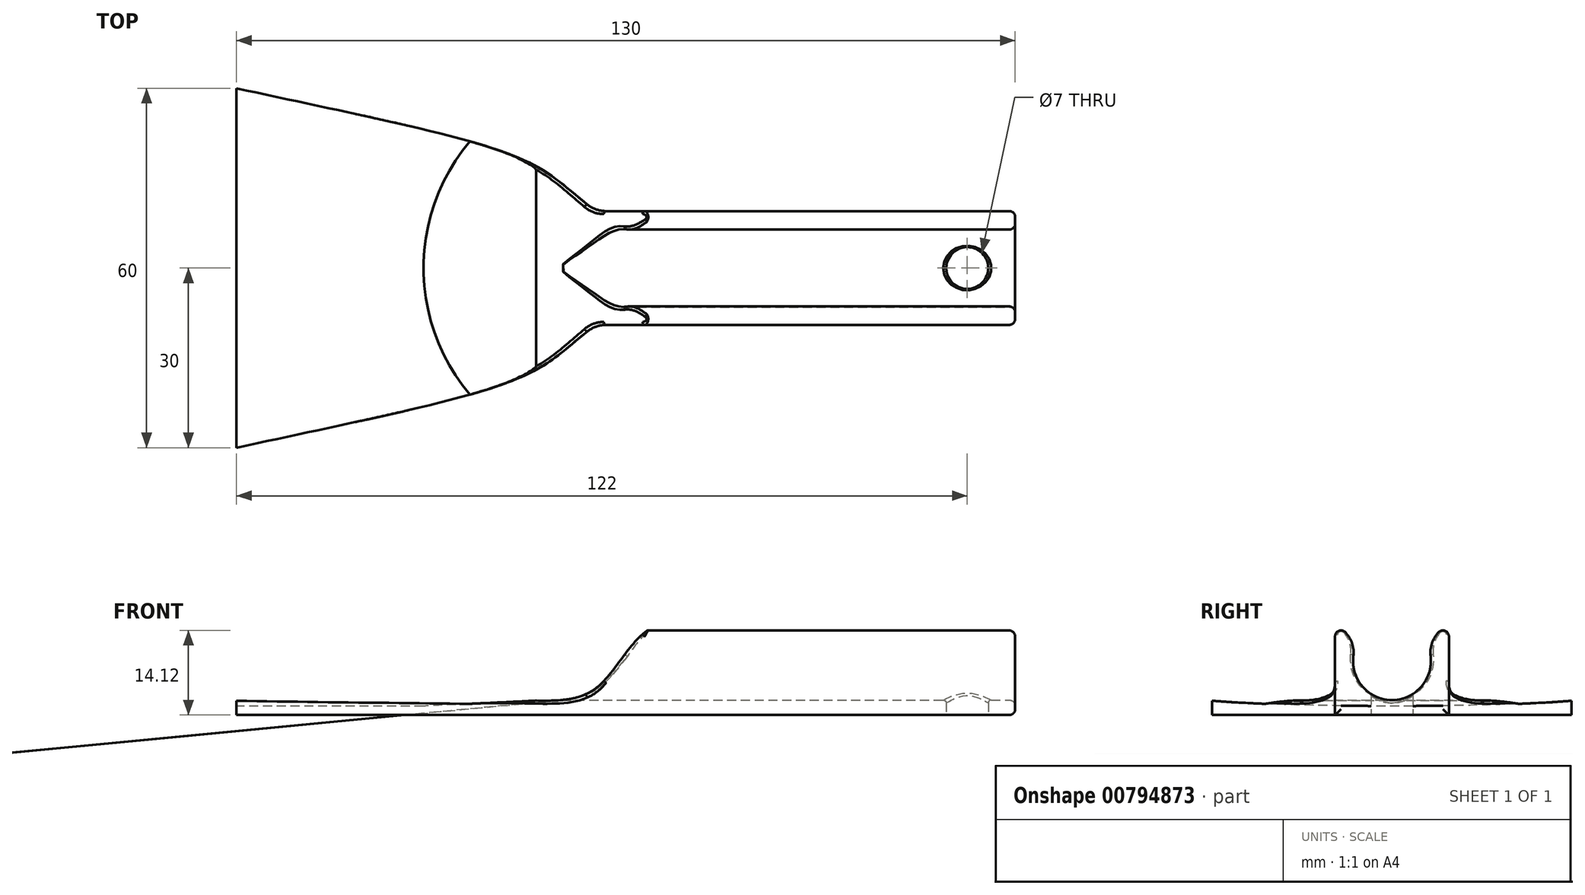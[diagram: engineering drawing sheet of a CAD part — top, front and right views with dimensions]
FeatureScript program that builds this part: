
annotation { "Feature Type Name" : "Feature", "Feature Type Description" : "" }
export const myFeature = defineFeature(function(context is Context, id is Id, definition is map)
    precondition{}
    {
        {
            var Q0;
            Q0=qCreatedBy(makeId("Top.planeOp"),FACE);
            var sketch = newSketch(context, id + "F0", { "sketchPlane" : qUnion([Q0])});
            skLineSegment(sketch, "E0.bottom", {"start": v(-35, 9.5) * mm, "end": v(35, 9.5) * mm});
            skLineSegment(sketch, "E0.top", {"start": v(-35, -9.5) * mm, "end": v(35, -9.5) * mm});
            skLineSegment(sketch, "E0.left", {"start": v(-35, 9.5) * mm, "end": v(-35, -9.5) * mm});
            skLineSegment(sketch, "E0.right", {"start": v(35, 9.5) * mm, "end": v(35, -9.5) * mm});
            skSolve(sketch);
        }
        {
            var Q0;
            Q0=makeQuery(id+"F0.imprint","IMPRINT",FACE,{"disambiguationData":[TD([[makeQuery(id+"F0.imprint","IMPRINT",EDGE,{"derivedFrom":sQuery(id+"F0.wireOp",EDGE,"E0.bottom")}),-1.0]])]});
            extrude(context, id + "F1", {"entities" : qUnion([Q0]), "depth" : 15 * mm, "offsetDistance" : 25 * mm});
        }
        {
            var Q0;
            Q0=qCreatedBy(makeId("Top.planeOp"),FACE);
            var sketch = newSketch(context, id + "F2", { "sketchPlane" : qUnion([Q0])});
            skFitSpline(sketch, "E1", {"points": [v(-35, 9.5) * mm, v(-45, 17) * mm, v(-95, 30) * mm], "startDerivative": vector(-36.4, 27.3) * mm, "endDerivative": vector(-124.24, 26.85) * mm});
            skLineSegment(sketch, "E2", {"start": v(-95, 30) * mm, "end": v(-95, 0) * mm});
            skLineSegment(sketch, "E3", {"start": v(-95, 0) * mm, "end": v(-35, 0) * mm});
            skLineSegment(sketch, "E4", {"start": v(-35, 0) * mm, "end": v(-35, 9.5) * mm});
            skSolve(sketch);
        }
        {
            var Q0;
            Q0=makeQuery(id+"F2.imprint","IMPRINT",FACE,{"disambiguationData":[TD([[makeQuery(id+"F2.imprint","IMPRINT",EDGE,{"derivedFrom":sQuery(id+"F2.wireOp",EDGE,"E1")}),1.0]])]});
            extrude(context, id + "F3", {"entities" : qUnion([Q0]), "operationType" : NewBodyOperationType.ADD, "depth" : 15 * mm, "offsetDistance" : 25 * mm});
        }
        {
            var Q0;
            Q0=makeQuery(id+"F1.opExtrude","SWEPT_BODY",BODY,{"disambiguationData":[OSD([sQuery(id+"F0.wireOp",EDGE,"E0.bottom"),sQuery(id+"F0.wireOp",EDGE,"E0.top"),sQuery(id+"F0.wireOp",EDGE,"E0.left"),sQuery(id+"F0.wireOp",EDGE,"E0.right")])]});
            var Q1;
            Q1=qCreatedBy(makeId("Front.planeOp"),FACE);
            mirror(context, id + "F4", {"operationType" : NewBodyOperationType.ADD, "entities" : qUnion([Q0]), "mirrorPlane" : qUnion([Q1])});
        }
        {
            var Q0;
            Q0=qCreatedBy(makeId("Front.planeOp"),FACE);
            var sketch = newSketch(context, id + "F5", { "sketchPlane" : qUnion([Q0])});
            skLineSegment(sketch, "E5", {"start": v(-50, 2.5) * mm, "end": v(-95, 2.5) * mm});
            skLineSegment(sketch, "E6", {"start": v(-95, 2.5) * mm, "end": v(-95, 15) * mm});
            skLineSegment(sketch, "E7", {"start": v(-95, 15) * mm, "end": v(-25, 15) * mm});
            skLineSegment(sketch, "E8", {"start": v(-50, 2.5) * mm, "end": v(-25, 15) * mm, "construction": true});
            skLineSegment(sketch, "E9", {"start": v(-37.5, 8.75) * mm, "end": v(-35.26, 4.28) * mm, "construction": true});
            skFitSpline(sketch, "E10", {"points": [v(-50, 2.5) * mm, v(-35.26, 4.28) * mm, v(-25, 15) * mm], "startDerivative": vector(36, 0) * mm, "endDerivative": vector(26.83, 13.42) * mm});
            skSolve(sketch);
        }
        {
            var Q0;
            Q0 = qSketchRegion(id + "F5", true);
            extrude(context, id + "F6", {"entities" : qUnion([Q0]), "operationType" : NewBodyOperationType.REMOVE, "endBound" : BoundingType.THROUGH_ALL, "oppositeDirection" : true, "depth" : 25 * mm, "offsetDistance" : 25 * mm, "hasSecondDirection" : true, "secondDirectionBound" : SecondDirectionBoundingType.THROUGH_ALL, "secondDirectionOppositeDirection" : false, "secondDirectionDepth" : 25 * mm});
        }
        {
            var Q0;
            Q0=makeQuery(id+"F1.opExtrude","SWEPT_FACE",FACE,{"disambiguationData":[OSD([sQuery(id+"F0.wireOp",EDGE,"E0.right")])]});
            var sketch = newSketch(context, id + "F7", { "sketchPlane" : qUnion([Q0])});
            skCircle(sketch, "E11", {"center": v(0, 9) * mm, "radius": 6.5 * mm});
            skSolve(sketch);
        }
        {
            var Q0;
            {var subQ0=sQuery(id+"F7.wireOp",EDGE,"E11");var subQ1=makeQuery(id+"F1.opExtrude","CAP_EDGE",EDGE,{"disambiguationData":[OSD([sQuery(id+"F0.wireOp",EDGE,"E0.right")])],"isStart":false});var subQ2=makeQuery(id+"F7.imprint","INTERSECT",VERTEX,{"disambiguationData":[OD(0.0)],"derivedFrom":[subQ1,subQ0]});Q0=makeQuery(id+"F7.imprint","IMPRINT",FACE,{"disambiguationData":[TD([[makeQuery(id+"F7.imprint","IMPRINT",EDGE,{"disambiguationData":[TD([[subQ2,1.0]])],"derivedFrom":subQ0}),1.0]])]});}
            var Q1;
            {var subQ0=sQuery(id+"F7.wireOp",EDGE,"E11");var subQ1=makeQuery(id+"F1.opExtrude","CAP_EDGE",EDGE,{"disambiguationData":[OSD([sQuery(id+"F0.wireOp",EDGE,"E0.right")])],"isStart":false});var subQ2=makeQuery(id+"F7.imprint","INTERSECT",VERTEX,{"disambiguationData":[OD(0.0)],"derivedFrom":[subQ1,subQ0]});Q1=makeQuery(id+"F7.imprint","IMPRINT",FACE,{"disambiguationData":[TD([[makeQuery(id+"F7.imprint","IMPRINT",EDGE,{"disambiguationData":[TD([[subQ2,-1.0]])],"derivedFrom":subQ0}),1.0]])]});}
            extrude(context, id + "F8", {"entities" : qUnion([Q0, Q1]), "operationType" : NewBodyOperationType.REMOVE, "endBound" : BoundingType.THROUGH_ALL, "oppositeDirection" : true, "depth" : 25 * mm, "offsetDistance" : 25 * mm});
        }
        {
            var Q0;
            {var subQ0=makeQuery(id+"F3.boolean.opBoolean","MERGE",FACE,{"derivedFrom":[makeQuery(id+"F1.opExtrude","CAP_FACE",FACE,{"disambiguationData":[OSD([sQuery(id+"F0.wireOp",EDGE,"E0.bottom"),sQuery(id+"F0.wireOp",EDGE,"E0.top"),sQuery(id+"F0.wireOp",EDGE,"E0.left"),sQuery(id+"F0.wireOp",EDGE,"E0.right")])],"isStart":false}),makeQuery(id+"F3.opExtrude","CAP_FACE",FACE,{"disambiguationData":[OSD([sQuery(id+"F2.wireOp",EDGE,"E1"),sQuery(id+"F2.wireOp",EDGE,"E2"),sQuery(id+"F2.wireOp",EDGE,"E3"),sQuery(id+"F2.wireOp",EDGE,"E4")])],"isStart":false})]});Q0=makeQuery(id+"F8.boolean.opBoolean","INTERSECT",EDGE,{"disambiguationData":[OD(1.0)],"derivedFrom":[makeQuery(id+"F4.boolean.opBoolean","MERGE",FACE,{"derivedFrom":[subQ0,makeQuery(id+"F4.opPattern","COPY",FACE,{"derivedFrom":subQ0,"instanceName":"1"})]}),makeQuery(id+"F8.opExtrude","SWEPT_FACE",FACE,{"disambiguationData":[OSD([sQuery(id+"F7.wireOp",EDGE,"E11")])]})]});}
            var Q1;
            {var subQ0=makeQuery(id+"F3.boolean.opBoolean","MERGE",FACE,{"derivedFrom":[makeQuery(id+"F1.opExtrude","CAP_FACE",FACE,{"disambiguationData":[OSD([sQuery(id+"F0.wireOp",EDGE,"E0.bottom"),sQuery(id+"F0.wireOp",EDGE,"E0.top"),sQuery(id+"F0.wireOp",EDGE,"E0.left"),sQuery(id+"F0.wireOp",EDGE,"E0.right")])],"isStart":false}),makeQuery(id+"F3.opExtrude","CAP_FACE",FACE,{"disambiguationData":[OSD([sQuery(id+"F2.wireOp",EDGE,"E1"),sQuery(id+"F2.wireOp",EDGE,"E2"),sQuery(id+"F2.wireOp",EDGE,"E3"),sQuery(id+"F2.wireOp",EDGE,"E4")])],"isStart":false})]});Q1=makeQuery(id+"F8.boolean.opBoolean","INTERSECT",EDGE,{"disambiguationData":[OD(0.0)],"derivedFrom":[makeQuery(id+"F4.boolean.opBoolean","MERGE",FACE,{"derivedFrom":[subQ0,makeQuery(id+"F4.opPattern","COPY",FACE,{"derivedFrom":subQ0,"instanceName":"1"})]}),makeQuery(id+"F8.opExtrude","SWEPT_FACE",FACE,{"disambiguationData":[OSD([sQuery(id+"F7.wireOp",EDGE,"E11")])]})]});}
            fillet(context, id + "F9", {"entities" : qUnion([Q0, Q1]), "radius" : 5 * mm, "tangentPropagation" : true, "allowEdgeOverflow" : false});
        }
        {
            var Q0;
            {var subQ0=sQuery(id+"F0.wireOp",EDGE,"E0.left");Q0=makeQuery(id+"F4.boolean.opBoolean","MERGE",EDGE,{"derivedFrom":[makeQuery(id+"F1.opExtrude","SWEPT_EDGE",EDGE,{"disambiguationData":[OSD([sQuery(id+"F0.wireOp",EDGE,"E0.top"),subQ0])]}),makeQuery(id+"F4.opPattern","COPY",EDGE,{"derivedFrom":makeQuery(id+"F3.boolean.opBoolean","MERGE",EDGE,{"derivedFrom":[makeQuery(id+"F1.opExtrude","SWEPT_EDGE",EDGE,{"disambiguationData":[OSD([sQuery(id+"F0.wireOp",EDGE,"E0.bottom"),subQ0])]}),makeQuery(id+"F3.opExtrude","SWEPT_EDGE",EDGE,{"disambiguationData":[OSD([sQuery(id+"F2.wireOp",EDGE,"E1"),sQuery(id+"F2.wireOp",EDGE,"E4")])]})]}),"instanceName":"1"})]});}
            var Q1;
            Q1=makeQuery(id+"F3.boolean.opBoolean","MERGE",EDGE,{"derivedFrom":[makeQuery(id+"F1.opExtrude","SWEPT_EDGE",EDGE,{"disambiguationData":[OSD([sQuery(id+"F0.wireOp",EDGE,"E0.bottom"),sQuery(id+"F0.wireOp",EDGE,"E0.left")])]}),makeQuery(id+"F3.opExtrude","SWEPT_EDGE",EDGE,{"disambiguationData":[OSD([sQuery(id+"F2.wireOp",EDGE,"E1"),sQuery(id+"F2.wireOp",EDGE,"E4")])]})]});
            fillet(context, id + "F10", {"entities" : qUnion([Q0, Q1]), "radius" : 5 * mm, "tangentPropagation" : true, "allowEdgeOverflow" : false});
        }
        {
            var Q0;
            {var subQ0=sQuery(id+"F0.wireOp",EDGE,"E0.top");var subQ1=makeQuery(id+"F3.boolean.opBoolean","MERGE",FACE,{"derivedFrom":[makeQuery(id+"F1.opExtrude","CAP_FACE",FACE,{"disambiguationData":[OSD([sQuery(id+"F0.wireOp",EDGE,"E0.bottom"),subQ0,sQuery(id+"F0.wireOp",EDGE,"E0.left"),sQuery(id+"F0.wireOp",EDGE,"E0.right")])],"isStart":false}),makeQuery(id+"F3.opExtrude","CAP_FACE",FACE,{"disambiguationData":[OSD([sQuery(id+"F2.wireOp",EDGE,"E1"),sQuery(id+"F2.wireOp",EDGE,"E2"),sQuery(id+"F2.wireOp",EDGE,"E3"),sQuery(id+"F2.wireOp",EDGE,"E4")])],"isStart":false})]});Q0=makeQuery(id+"F9.opFillet","BLEND_EDGE",EDGE,{"blendedFrom":[makeQuery(id+"F8.boolean.opBoolean","INTERSECT",EDGE,{"disambiguationData":[OD(1.0)],"derivedFrom":[makeQuery(id+"F4.boolean.opBoolean","MERGE",FACE,{"derivedFrom":[subQ1,makeQuery(id+"F4.opPattern","COPY",FACE,{"derivedFrom":subQ1,"instanceName":"1"})]}),makeQuery(id+"F8.opExtrude","SWEPT_FACE",FACE,{"disambiguationData":[OSD([sQuery(id+"F7.wireOp",EDGE,"E11")])]})]}),makeQuery(id+"F1.opExtrude","SWEPT_FACE",FACE,{"disambiguationData":[OSD([subQ0])]})],"blendedInto":[makeQuery(id+"F1.opExtrude","SWEPT_FACE",FACE,{"disambiguationData":[OSD([subQ0])]})]});}
            var Q1;
            {var subQ0=sQuery(id+"F0.wireOp",EDGE,"E0.bottom");var subQ1=makeQuery(id+"F3.boolean.opBoolean","MERGE",FACE,{"derivedFrom":[makeQuery(id+"F1.opExtrude","CAP_FACE",FACE,{"disambiguationData":[OSD([subQ0,sQuery(id+"F0.wireOp",EDGE,"E0.top"),sQuery(id+"F0.wireOp",EDGE,"E0.left"),sQuery(id+"F0.wireOp",EDGE,"E0.right")])],"isStart":false}),makeQuery(id+"F3.opExtrude","CAP_FACE",FACE,{"disambiguationData":[OSD([sQuery(id+"F2.wireOp",EDGE,"E1"),sQuery(id+"F2.wireOp",EDGE,"E2"),sQuery(id+"F2.wireOp",EDGE,"E3"),sQuery(id+"F2.wireOp",EDGE,"E4")])],"isStart":false})]});Q1=makeQuery(id+"F9.opFillet","BLEND_EDGE",EDGE,{"blendedFrom":[makeQuery(id+"F8.boolean.opBoolean","INTERSECT",EDGE,{"disambiguationData":[OD(0.0)],"derivedFrom":[makeQuery(id+"F4.boolean.opBoolean","MERGE",FACE,{"derivedFrom":[subQ1,makeQuery(id+"F4.opPattern","COPY",FACE,{"derivedFrom":subQ1,"instanceName":"1"})]}),makeQuery(id+"F8.opExtrude","SWEPT_FACE",FACE,{"disambiguationData":[OSD([sQuery(id+"F7.wireOp",EDGE,"E11")])]})]}),makeQuery(id+"F1.opExtrude","SWEPT_FACE",FACE,{"disambiguationData":[OSD([subQ0])]})],"blendedInto":[makeQuery(id+"F1.opExtrude","SWEPT_FACE",FACE,{"disambiguationData":[OSD([subQ0])]})]});}
            fillet(context, id + "F11", {"entities" : qUnion([Q0, Q1]), "radius" : 1 * mm, "tangentPropagation" : true, "allowEdgeOverflow" : false});
        }
        {
            var Q0;
            Q0=qCreatedBy(makeId("Top.planeOp"),FACE);
            var sketch = newSketch(context, id + "F12", { "sketchPlane" : qUnion([Q0])});
            skCircle(sketch, "E12", {"center": v(27, 0) * mm, "radius": 3.5 * mm});
            skSolve(sketch);
        }
        {
            var Q0;
            Q0=makeQuery(id+"F12.imprint","IMPRINT",FACE,{"disambiguationData":[TD([[makeQuery(id+"F12.imprint","IMPRINT",EDGE,{"derivedFrom":sQuery(id+"F12.wireOp",EDGE,"E12")}),1.0]])]});
            extrude(context, id + "F13", {"entities" : qUnion([Q0]), "operationType" : NewBodyOperationType.REMOVE, "endBound" : BoundingType.THROUGH_ALL, "depth" : 25 * mm, "offsetDistance" : 25 * mm});
        }
        {
            var Q0;
            Q0=makeQuery(id+"F13.boolean.opBoolean","INTERSECT",EDGE,{"derivedFrom":[makeQuery(id+"F8.boolean.opBoolean","COPY",FACE,{"derivedFrom":makeQuery(id+"F8.opExtrude","SWEPT_FACE",FACE,{"disambiguationData":[OSD([sQuery(id+"F7.wireOp",EDGE,"E11")])]})}),makeQuery(id+"F13.opExtrude","SWEPT_FACE",FACE,{"disambiguationData":[OSD([sQuery(id+"F12.wireOp",EDGE,"E12")])]})]});
            fillet(context, id + "F14", {"entities" : qUnion([Q0]), "radius" : 0.5 * mm, "tangentPropagation" : true, "defaultsChanged" : false, "vertexSettings" : [], "allowEdgeOverflow" : false});
        }
        {
            var Q0;
            Q0=makeQuery(id+"F1.opExtrude","SWEPT_FACE",FACE,{"disambiguationData":[OSD([sQuery(id+"F0.wireOp",EDGE,"E0.right")])]});
            fillet(context, id + "F15", {"entities" : qUnion([Q0]), "radius" : 1 * mm, "tangentPropagation" : true, "allowEdgeOverflow" : false});
        }
        {
            var Q0;
            {var subQ0=makeQuery(id+"F3.opExtrude","SWEPT_FACE",FACE,{"disambiguationData":[OSD([sQuery(id+"F2.wireOp",EDGE,"E2")])]});Q0=makeQuery(id+"F4.boolean.opBoolean","MERGE",FACE,{"derivedFrom":[subQ0,makeQuery(id+"F4.opPattern","COPY",FACE,{"derivedFrom":subQ0,"instanceName":"1"})]});}
            var sketch = newSketch(context, id + "F16", { "sketchPlane" : qUnion([Q0])});
            skLineSegment(sketch, "E13", {"start": v(-35, 3) * mm, "end": v(35, 3) * mm});
            skFitSpline(sketch, "E14", {"points": [v(-35, 3) * mm, v(0, 1.5) * mm, v(35, 3) * mm], "startDerivative": vector(30, -6) * mm, "endDerivative": vector(30, 6) * mm});
            skSolve(sketch);
        }
        {
            var Q0;
            Q0 = qSketchRegion(id + "F16", true);
            extrude(context, id + "F17", {"entities" : qUnion([Q0]), "operationType" : NewBodyOperationType.REMOVE, "oppositeDirection" : true, "depth" : 30 * mm, "offsetDistance" : 25 * mm});
        }
        {
            var Q0;
            Q0=makeQuery(id+"F17.boolean.opBoolean","INTERSECT",EDGE,{"derivedFrom":[makeQuery(id+"F6.boolean.opBoolean","COPY",FACE,{"derivedFrom":makeQuery(id+"F6.opExtrude","SWEPT_FACE",FACE,{"disambiguationData":[OSD([sQuery(id+"F5.wireOp",EDGE,"E5")])]})}),makeQuery(id+"F17.opExtrude","CAP_FACE",FACE,{"disambiguationData":[OSD([sQuery(id+"F16.wireOp",EDGE,"E13"),sQuery(id+"F16.wireOp",EDGE,"E14")])],"isStart":false})]});
            chamfer(context, id + "F18", {"entities" : qUnion([Q0]), "chamferType" : ChamferType.OFFSET_ANGLE, "width" : 20 * mm, "oppositeDirection" : false, "angle" : 2.75 * degree, "tangentPropagation" : true});
        }
        {
            var Q0;
            Q0=makeQuery(id+"F6.boolean.opBoolean","INTERSECT",EDGE,{"derivedFrom":[makeQuery(id+"F1.opExtrude","SWEPT_FACE",FACE,{"disambiguationData":[OSD([sQuery(id+"F0.wireOp",EDGE,"E0.bottom")])]}),makeQuery(id+"F6.opExtrude","SWEPT_FACE",FACE,{"disambiguationData":[OSD([sQuery(id+"F5.wireOp",EDGE,"E10")])]})]});
            var Q1;
            {var subQ0=sQuery(id+"F2.wireOp",EDGE,"E4");var subQ1=sQuery(id+"F2.wireOp",EDGE,"E1");var subQ2=sQuery(id+"F0.wireOp",EDGE,"E0.left");var subQ3=sQuery(id+"F0.wireOp",EDGE,"E0.bottom");var subQ4=makeQuery(id+"F3.boolean.opBoolean","MERGE",FACE,{"derivedFrom":[makeQuery(id+"F1.opExtrude","CAP_FACE",FACE,{"disambiguationData":[OSD([subQ3,sQuery(id+"F0.wireOp",EDGE,"E0.top"),subQ2,sQuery(id+"F0.wireOp",EDGE,"E0.right")])],"isStart":true}),makeQuery(id+"F3.opExtrude","CAP_FACE",FACE,{"disambiguationData":[OSD([subQ1,sQuery(id+"F2.wireOp",EDGE,"E2"),sQuery(id+"F2.wireOp",EDGE,"E3"),subQ0])],"isStart":true})]});Q1=makeQuery(id+"FUEg22sjh9F5Z2j_1.opFillet","BLEND_EDGE",EDGE,{"disambiguationData":[OD(0.0)],"blendedFrom":[makeQuery(id+"F10.opFillet","BLEND_EDGE",EDGE,{"blendedFrom":[makeQuery(id+"F3.boolean.opBoolean","MERGE",EDGE,{"derivedFrom":[makeQuery(id+"F1.opExtrude","SWEPT_EDGE",EDGE,{"disambiguationData":[OSD([subQ3,subQ2])]}),makeQuery(id+"F3.opExtrude","SWEPT_EDGE",EDGE,{"disambiguationData":[OSD([subQ1,subQ0])]})]}),makeQuery(id+"F4.boolean.opBoolean","MERGE",FACE,{"derivedFrom":[subQ4,makeQuery(id+"F4.opPattern","COPY",FACE,{"derivedFrom":subQ4,"instanceName":"1"})]})],"blendedInto":[makeQuery(id+"F4.boolean.opBoolean","MERGE",FACE,{"derivedFrom":[subQ4,makeQuery(id+"F4.opPattern","COPY",FACE,{"derivedFrom":subQ4,"instanceName":"1"})]})]}),makeQuery(id+"F6.boolean.opBoolean","COPY",FACE,{"derivedFrom":makeQuery(id+"F6.opExtrude","SWEPT_FACE",FACE,{"disambiguationData":[OSD([sQuery(id+"F5.wireOp",EDGE,"E10")])]})})],"blendedInto":[makeQuery(id+"F6.boolean.opBoolean","COPY",FACE,{"derivedFrom":makeQuery(id+"F6.opExtrude","SWEPT_FACE",FACE,{"disambiguationData":[OSD([sQuery(id+"F5.wireOp",EDGE,"E10")])]})})]});}
            var Q2;
            {var subQ0=sQuery(id+"F2.wireOp",EDGE,"E4");var subQ1=sQuery(id+"F2.wireOp",EDGE,"E1");var subQ2=sQuery(id+"F0.wireOp",EDGE,"E0.left");var subQ3=sQuery(id+"F0.wireOp",EDGE,"E0.bottom");var subQ4=makeQuery(id+"F3.boolean.opBoolean","MERGE",FACE,{"derivedFrom":[makeQuery(id+"F1.opExtrude","CAP_FACE",FACE,{"disambiguationData":[OSD([subQ3,sQuery(id+"F0.wireOp",EDGE,"E0.top"),subQ2,sQuery(id+"F0.wireOp",EDGE,"E0.right")])],"isStart":true}),makeQuery(id+"F3.opExtrude","CAP_FACE",FACE,{"disambiguationData":[OSD([subQ1,sQuery(id+"F2.wireOp",EDGE,"E2"),sQuery(id+"F2.wireOp",EDGE,"E3"),subQ0])],"isStart":true})]});Q2=makeQuery(id+"FUEg22sjh9F5Z2j_1.opFillet","BLEND_EDGE",EDGE,{"disambiguationData":[OD(1.0)],"blendedFrom":[makeQuery(id+"F10.opFillet","BLEND_EDGE",EDGE,{"blendedFrom":[makeQuery(id+"F3.boolean.opBoolean","MERGE",EDGE,{"derivedFrom":[makeQuery(id+"F1.opExtrude","SWEPT_EDGE",EDGE,{"disambiguationData":[OSD([subQ3,subQ2])]}),makeQuery(id+"F3.opExtrude","SWEPT_EDGE",EDGE,{"disambiguationData":[OSD([subQ1,subQ0])]})]}),makeQuery(id+"F4.boolean.opBoolean","MERGE",FACE,{"derivedFrom":[subQ4,makeQuery(id+"F4.opPattern","COPY",FACE,{"derivedFrom":subQ4,"instanceName":"1"})]})],"blendedInto":[makeQuery(id+"F4.boolean.opBoolean","MERGE",FACE,{"derivedFrom":[subQ4,makeQuery(id+"F4.opPattern","COPY",FACE,{"derivedFrom":subQ4,"instanceName":"1"})]})]}),makeQuery(id+"F6.boolean.opBoolean","COPY",FACE,{"derivedFrom":makeQuery(id+"F6.opExtrude","SWEPT_FACE",FACE,{"disambiguationData":[OSD([sQuery(id+"F5.wireOp",EDGE,"E10")])]})})],"blendedInto":[makeQuery(id+"F6.boolean.opBoolean","COPY",FACE,{"derivedFrom":makeQuery(id+"F6.opExtrude","SWEPT_FACE",FACE,{"disambiguationData":[OSD([sQuery(id+"F5.wireOp",EDGE,"E10")])]})})]});}
            var Q3;
            {var subQ0=sQuery(id+"F2.wireOp",EDGE,"E4");var subQ1=sQuery(id+"F2.wireOp",EDGE,"E1");var subQ2=sQuery(id+"F0.wireOp",EDGE,"E0.left");var subQ3=sQuery(id+"F0.wireOp",EDGE,"E0.top");var subQ4=sQuery(id+"F0.wireOp",EDGE,"E0.bottom");var subQ5=makeQuery(id+"F3.boolean.opBoolean","MERGE",FACE,{"derivedFrom":[makeQuery(id+"F1.opExtrude","CAP_FACE",FACE,{"disambiguationData":[OSD([subQ4,subQ3,subQ2,sQuery(id+"F0.wireOp",EDGE,"E0.right")])],"isStart":true}),makeQuery(id+"F3.opExtrude","CAP_FACE",FACE,{"disambiguationData":[OSD([subQ1,sQuery(id+"F2.wireOp",EDGE,"E2"),sQuery(id+"F2.wireOp",EDGE,"E3"),subQ0])],"isStart":true})]});Q3=makeQuery(id+"FUEg22sjh9F5Z2j_1.opFillet","BLEND_EDGE",EDGE,{"disambiguationData":[OD(1.0)],"blendedFrom":[makeQuery(id+"F10.opFillet","BLEND_EDGE",EDGE,{"blendedFrom":[makeQuery(id+"F4.boolean.opBoolean","MERGE",EDGE,{"derivedFrom":[makeQuery(id+"F1.opExtrude","SWEPT_EDGE",EDGE,{"disambiguationData":[OSD([subQ3,subQ2])]}),makeQuery(id+"F4.opPattern","COPY",EDGE,{"derivedFrom":makeQuery(id+"F3.boolean.opBoolean","MERGE",EDGE,{"derivedFrom":[makeQuery(id+"F1.opExtrude","SWEPT_EDGE",EDGE,{"disambiguationData":[OSD([subQ4,subQ2])]}),makeQuery(id+"F3.opExtrude","SWEPT_EDGE",EDGE,{"disambiguationData":[OSD([subQ1,subQ0])]})]}),"instanceName":"1"})]}),makeQuery(id+"F4.boolean.opBoolean","MERGE",FACE,{"derivedFrom":[subQ5,makeQuery(id+"F4.opPattern","COPY",FACE,{"derivedFrom":subQ5,"instanceName":"1"})]})],"blendedInto":[makeQuery(id+"F4.boolean.opBoolean","MERGE",FACE,{"derivedFrom":[subQ5,makeQuery(id+"F4.opPattern","COPY",FACE,{"derivedFrom":subQ5,"instanceName":"1"})]})]}),makeQuery(id+"F6.boolean.opBoolean","COPY",FACE,{"derivedFrom":makeQuery(id+"F6.opExtrude","SWEPT_FACE",FACE,{"disambiguationData":[OSD([sQuery(id+"F5.wireOp",EDGE,"E10")])]})})],"blendedInto":[makeQuery(id+"F6.boolean.opBoolean","COPY",FACE,{"derivedFrom":makeQuery(id+"F6.opExtrude","SWEPT_FACE",FACE,{"disambiguationData":[OSD([sQuery(id+"F5.wireOp",EDGE,"E10")])]})})]});}
            var Q4;
            {var subQ0=sQuery(id+"F2.wireOp",EDGE,"E4");var subQ1=sQuery(id+"F2.wireOp",EDGE,"E1");var subQ2=sQuery(id+"F0.wireOp",EDGE,"E0.left");var subQ3=sQuery(id+"F0.wireOp",EDGE,"E0.top");var subQ4=sQuery(id+"F0.wireOp",EDGE,"E0.bottom");var subQ5=makeQuery(id+"F3.boolean.opBoolean","MERGE",FACE,{"derivedFrom":[makeQuery(id+"F1.opExtrude","CAP_FACE",FACE,{"disambiguationData":[OSD([subQ4,subQ3,subQ2,sQuery(id+"F0.wireOp",EDGE,"E0.right")])],"isStart":true}),makeQuery(id+"F3.opExtrude","CAP_FACE",FACE,{"disambiguationData":[OSD([subQ1,sQuery(id+"F2.wireOp",EDGE,"E2"),sQuery(id+"F2.wireOp",EDGE,"E3"),subQ0])],"isStart":true})]});Q4=makeQuery(id+"FUEg22sjh9F5Z2j_1.opFillet","BLEND_EDGE",EDGE,{"disambiguationData":[OD(0.0)],"blendedFrom":[makeQuery(id+"F10.opFillet","BLEND_EDGE",EDGE,{"blendedFrom":[makeQuery(id+"F4.boolean.opBoolean","MERGE",EDGE,{"derivedFrom":[makeQuery(id+"F1.opExtrude","SWEPT_EDGE",EDGE,{"disambiguationData":[OSD([subQ3,subQ2])]}),makeQuery(id+"F4.opPattern","COPY",EDGE,{"derivedFrom":makeQuery(id+"F3.boolean.opBoolean","MERGE",EDGE,{"derivedFrom":[makeQuery(id+"F1.opExtrude","SWEPT_EDGE",EDGE,{"disambiguationData":[OSD([subQ4,subQ2])]}),makeQuery(id+"F3.opExtrude","SWEPT_EDGE",EDGE,{"disambiguationData":[OSD([subQ1,subQ0])]})]}),"instanceName":"1"})]}),makeQuery(id+"F4.boolean.opBoolean","MERGE",FACE,{"derivedFrom":[subQ5,makeQuery(id+"F4.opPattern","COPY",FACE,{"derivedFrom":subQ5,"instanceName":"1"})]})],"blendedInto":[makeQuery(id+"F4.boolean.opBoolean","MERGE",FACE,{"derivedFrom":[subQ5,makeQuery(id+"F4.opPattern","COPY",FACE,{"derivedFrom":subQ5,"instanceName":"1"})]})]}),makeQuery(id+"F6.boolean.opBoolean","COPY",FACE,{"derivedFrom":makeQuery(id+"F6.opExtrude","SWEPT_FACE",FACE,{"disambiguationData":[OSD([sQuery(id+"F5.wireOp",EDGE,"E10")])]})})],"blendedInto":[makeQuery(id+"F6.boolean.opBoolean","COPY",FACE,{"derivedFrom":makeQuery(id+"F6.opExtrude","SWEPT_FACE",FACE,{"disambiguationData":[OSD([sQuery(id+"F5.wireOp",EDGE,"E10")])]})})]});}
            var Q5;
            Q5=makeQuery(id+"F6.boolean.opBoolean","INTERSECT",EDGE,{"derivedFrom":[makeQuery(id+"F1.opExtrude","SWEPT_FACE",FACE,{"disambiguationData":[OSD([sQuery(id+"F0.wireOp",EDGE,"E0.top")])]}),makeQuery(id+"F6.opExtrude","SWEPT_FACE",FACE,{"disambiguationData":[OSD([sQuery(id+"F5.wireOp",EDGE,"E10")])]})]});
            var Q6;
            Q6=makeQuery(id+"FUEg22sjh9F5Z2j_1.opFillet","BLEND_EDGE",EDGE,{"blendedFrom":[makeQuery(id+"F4.opPattern","COPY",EDGE,{"derivedFrom":makeQuery(id+"F3.opExtrude","CAP_EDGE",EDGE,{"disambiguationData":[OSD([sQuery(id+"F2.wireOp",EDGE,"E1")])],"isStart":true}),"instanceName":"1"}),makeQuery(id+"F6.boolean.opBoolean","COPY",FACE,{"derivedFrom":makeQuery(id+"F6.opExtrude","SWEPT_FACE",FACE,{"disambiguationData":[OSD([sQuery(id+"F5.wireOp",EDGE,"E10")])]})})],"blendedInto":[makeQuery(id+"F6.boolean.opBoolean","COPY",FACE,{"derivedFrom":makeQuery(id+"F6.opExtrude","SWEPT_FACE",FACE,{"disambiguationData":[OSD([sQuery(id+"F5.wireOp",EDGE,"E10")])]})})]});
            fillet(context, id + "F19", {"entities" : qUnion([Q0, Q1, Q2, Q3, Q4, Q5, Q6]), "radius" : 0.5 * mm, "tangentPropagation" : true, "allowEdgeOverflow" : false});
        }
    });
